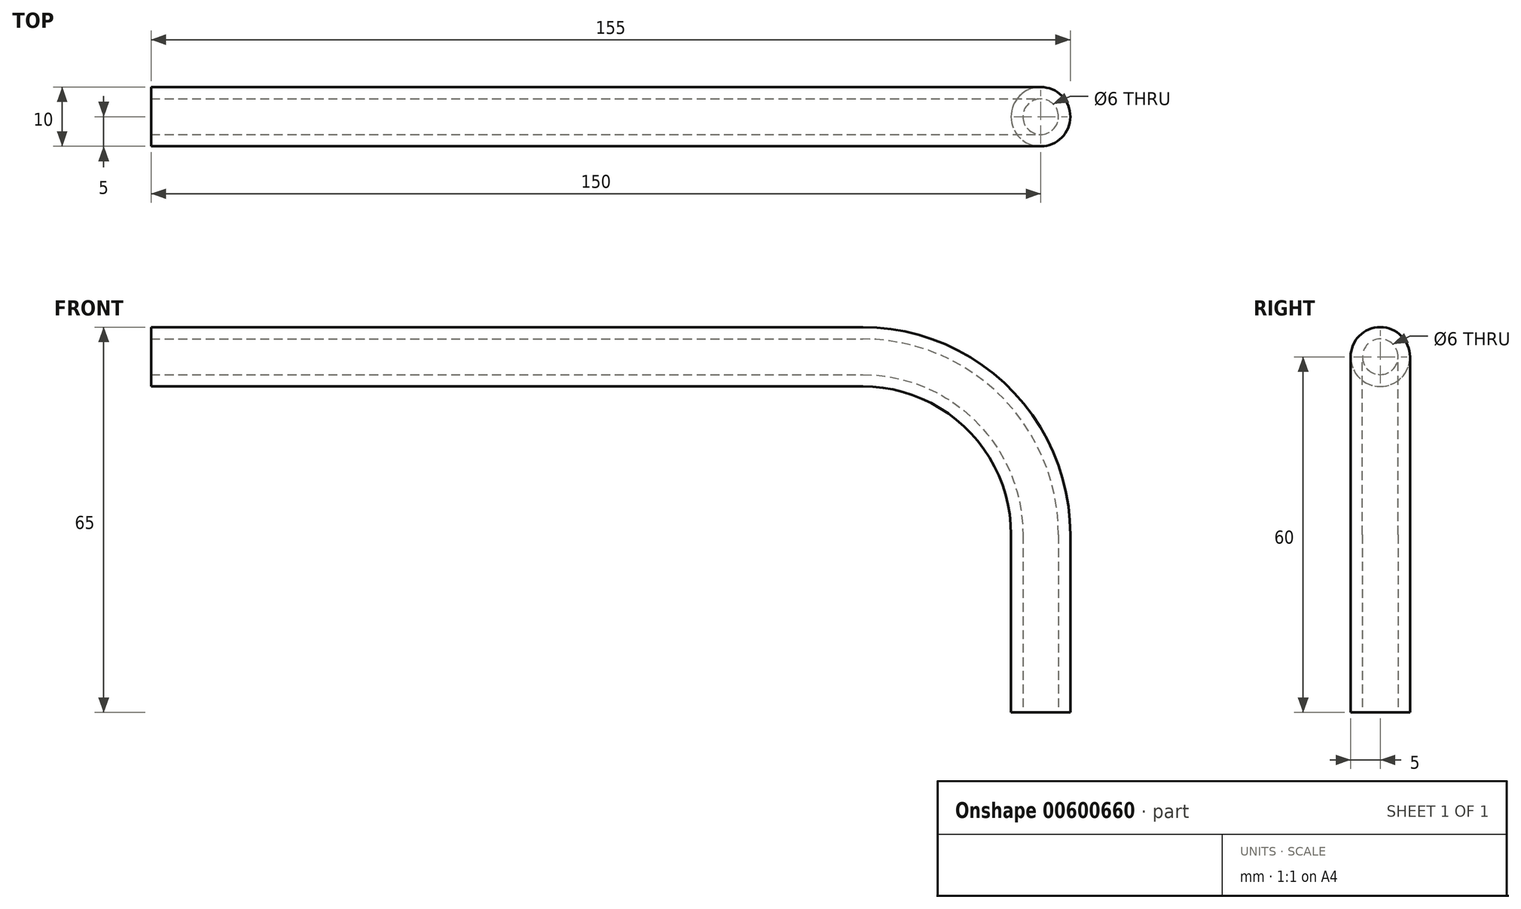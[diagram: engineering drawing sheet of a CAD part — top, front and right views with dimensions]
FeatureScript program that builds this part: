
annotation { "Feature Type Name" : "Feature", "Feature Type Description" : "" }
export const myFeature = defineFeature(function(context is Context, id is Id, definition is map)
    precondition{}
    {
        {
            var Q0;
            Q0=qCreatedBy(makeId("Right.planeOp"),FACE);
            var sketch = newSketch(context, id + "F0", { "sketchPlane" : qUnion([Q0])});
            skCircle(sketch, "E0", {"center": v(0, 0) * mm, "radius": 3 * mm});
            skCircle(sketch, "E1", {"center": v(0, 0) * mm, "radius": 5 * mm});
            skSolve(sketch);
        }
        {
            var Q0;
            Q0=makeQuery(id+"F0.imprint","IMPRINT",FACE,{"disambiguationData":[TD([[makeQuery(id+"F0.imprint","IMPRINT",EDGE,{"derivedFrom":sQuery(id+"F0.wireOp",EDGE,"E0")}),-1.0]])]});
            extrude(context, id + "F1", {"entities" : qUnion([Q0]), "oppositeDirection" : true, "depth" : 120 * mm, "offsetDistance" : 25 * mm});
        }
        {
            var Q0;
            Q0=qCreatedBy(makeId("Front.planeOp"),FACE);
            var sketch = newSketch(context, id + "F2", { "sketchPlane" : qUnion([Q0])});
            skPoint(sketch, "E2", {"position": v(0, -30) * mm});
            skArc(sketch, "E3", {"start": v(0, 0) * mm, "mid": v(21.21, -8.79) * mm, "end": v(30, -30) * mm});
            skLineSegment(sketch, "E4", {"start": v(30, -30) * mm, "end": v(30, -60) * mm});
            skSolve(sketch);
        }
        {
            var Q0;
            Q0=makeQuery(id+"F1.opExtrude","CAP_FACE",FACE,{"disambiguationData":[OSD([sQuery(id+"F0.wireOp",EDGE,"E0"),sQuery(id+"F0.wireOp",EDGE,"E1")])],"isStart":true});
            var Q1;
            Q1=sQuery(id+"F2.wireOp",EDGE,"E3");
            var Q2;
            Q2=sQuery(id+"F2.wireOp",EDGE,"E4");
            sweep(context, id + "F3", {"operationType" : NewBodyOperationType.ADD, "profiles" : qUnion([Q0]), "path" : qUnion([Q1, Q2])});
        }
    });
